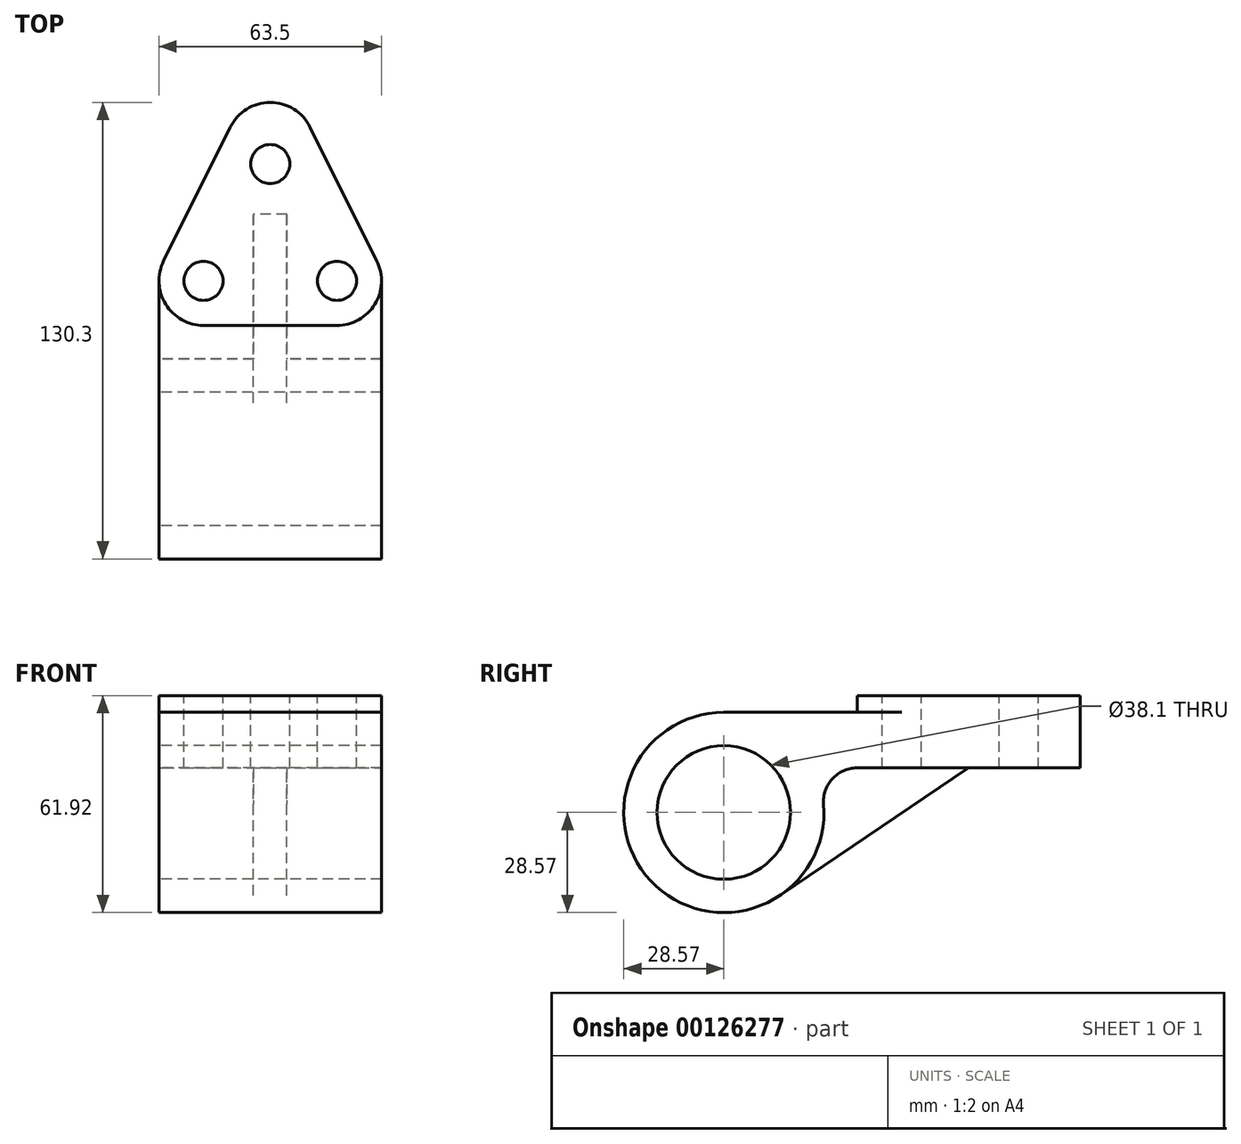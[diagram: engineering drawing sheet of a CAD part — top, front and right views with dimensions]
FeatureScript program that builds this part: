
annotation { "Feature Type Name" : "Feature", "Feature Type Description" : "" }
export const myFeature = defineFeature(function(context is Context, id is Id, definition is map)
    precondition{}
    {
        {
            var Q0;
            Q0=qCreatedBy(makeId("Right.planeOp"),FACE);
            var sketch = newSketch(context, id + "F0", { "sketchPlane" : qUnion([Q0])});
            skArc(sketch, "E0", {"start": v(0, 28.58) * mm, "mid": v(-19.35, -21.03) * mm, "end": v(28.48, 2.38) * mm});
            skCircle(sketch, "E1", {"center": v(0, 0) * mm, "radius": 19.05 * mm});
            skLineSegment(sketch, "E2", {"start": v(0, 28.58) * mm, "end": v(38.1, 28.58) * mm});
            skLineSegment(sketch, "E3", {"start": v(38.1, 28.58) * mm, "end": v(38.1, 33.35) * mm});
            skLineSegment(sketch, "E4", {"start": v(38.1, 33.35) * mm, "end": v(101.73, 33.35) * mm});
            skLineSegment(sketch, "E5", {"start": v(101.73, 33.35) * mm, "end": v(101.73, 12.7) * mm});
            skLineSegment(sketch, "E6", {"start": v(101.73, 12.7) * mm, "end": v(37.97, 12.7) * mm});
            skPoint(sketch, "E7.visualSharp", {"position": v(25.6, 12.7) * mm});
            skArc(sketch, "E7.filletArc", {"start": v(37.97, 12.7) * mm, "mid": v(30.96, 9.62) * mm, "end": v(28.48, 2.38) * mm});
            skLineSegment(sketch, "E8", {"start": v(69.85, 12.7) * mm, "end": v(69.85, 33.35) * mm, "construction": true});
            skLineSegment(sketch, "E9", {"start": v(16, -23.68) * mm, "end": v(69.85, 12.7) * mm});
            skSolve(sketch);
        }
        {
            var Q0;
            Q0=makeQuery(id+"F0.imprint","IMPRINT",FACE,{"disambiguationData":[TD([[makeQuery(id+"F0.imprint","IMPRINT",EDGE,{"derivedFrom":sQuery(id+"F0.wireOp",EDGE,"E1")}),-1.0]])]});
            extrude(context, id + "F1", {"entities" : qUnion([Q0]), "endBound" : BoundingType.SYMMETRIC, "depth" : 63.5 * mm});
        }
        {
            var Q0;
            Q0=makeQuery(id+"F1.opExtrude","SWEPT_FACE",FACE,{"disambiguationData":[OSD([sQuery(id+"F0.wireOp",EDGE,"E4")])]});
            var sketch = newSketch(context, id + "F2", { "sketchPlane" : qUnion([Q0])});
            skCircle(sketch, "E10", {"center": v(0, 84.15) * mm, "radius": 5.56 * mm});
            skCircle(sketch, "E11", {"center": v(-19.05, 50.8) * mm, "radius": 5.56 * mm});
            skCircle(sketch, "E12", {"center": v(19.05, 50.8) * mm, "radius": 5.56 * mm});
            skLineSegment(sketch, "E13", {"start": v(-19.05, 38.1) * mm, "end": v(19.05, 38.1) * mm});
            skArc(sketch, "E14", {"start": v(19.05, 38.1) * mm, "mid": v(29.85, 44.12) * mm, "end": v(30.42, 56.46) * mm});
            skArc(sketch, "E15", {"start": v(-30.42, 56.46) * mm, "mid": v(-29.85, 44.12) * mm, "end": v(-19.05, 38.1) * mm});
            skArc(sketch, "E16", {"start": v(11.37, 94.7) * mm, "mid": v(0, 101.73) * mm, "end": v(-11.37, 94.7) * mm});
            skLineSegment(sketch, "E17", {"start": v(-11.37, 94.7) * mm, "end": v(-30.42, 56.46) * mm});
            skLineSegment(sketch, "E18", {"start": v(30.42, 56.46) * mm, "end": v(11.37, 94.7) * mm});
            skSolve(sketch);
        }
        {
            var Q0;
            {var subQ0=sQuery(id+"F2.wireOp",EDGE,"E18");Q0=makeQuery(id+"F2.imprint","IMPRINT",FACE,{"disambiguationData":[TD([[makeQuery(id+"F2.imprint","IMPRINT",EDGE,{"derivedFrom":subQ0}),-1.0]])]});}
            extrude(context, id + "F3", {"entities" : qUnion([Q0]), "operationType" : NewBodyOperationType.REMOVE, "oppositeDirection" : true, "depth" : 43.07 * mm});
        }
        {
            var Q0;
            {var subQ0=sQuery(id+"F2.wireOp",EDGE,"E17");Q0=makeQuery(id+"F2.imprint","IMPRINT",FACE,{"disambiguationData":[TD([[makeQuery(id+"F2.imprint","IMPRINT",EDGE,{"derivedFrom":subQ0}),-1.0]])]});}
            extrude(context, id + "F4", {"entities" : qUnion([Q0]), "operationType" : NewBodyOperationType.REMOVE, "oppositeDirection" : true, "depth" : 25.4 * mm});
        }
        {
            var Q0;
            {var subQ0=sQuery(id+"F2.wireOp",EDGE,"E15");var subQ1=sQuery(id+"F0.wireOp",EDGE,"E4");var subQ4=makeQuery(id+"F1.opExtrude","CAP_EDGE",EDGE,{"disambiguationData":[OSD([subQ1])],"isStart":true});var subQ5=makeQuery(id+"F2.imprint","INTERSECT",VERTEX,{"derivedFrom":[subQ4,subQ0]});Q0=makeQuery(id+"F2.imprint","IMPRINT",FACE,{"disambiguationData":[TD([[makeQuery(id+"F2.imprint","IMPRINT",EDGE,{"disambiguationData":[TD([[subQ5,1.0]])],"derivedFrom":subQ4}),-1.0]])]});}
            extrude(context, id + "F5", {"entities" : qUnion([Q0]), "operationType" : NewBodyOperationType.REMOVE, "oppositeDirection" : true, "depth" : 4.78 * mm});
        }
        {
            var Q0;
            {var subQ0=sQuery(id+"F2.wireOp",EDGE,"E14");var subQ1=sQuery(id+"F0.wireOp",EDGE,"E4");var subQ4=makeQuery(id+"F1.opExtrude","CAP_EDGE",EDGE,{"disambiguationData":[OSD([subQ1])],"isStart":false});var subQ5=makeQuery(id+"F2.imprint","INTERSECT",VERTEX,{"derivedFrom":[subQ4,subQ0]});Q0=makeQuery(id+"F2.imprint","IMPRINT",FACE,{"disambiguationData":[TD([[makeQuery(id+"F2.imprint","IMPRINT",EDGE,{"disambiguationData":[TD([[subQ5,1.0]])],"derivedFrom":subQ4}),1.0]])]});}
            extrude(context, id + "F6", {"entities" : qUnion([Q0]), "operationType" : NewBodyOperationType.REMOVE, "oppositeDirection" : true, "depth" : 4.78 * mm});
        }
        {
            var Q0;
            Q0=makeQuery(id+"F2.imprint","IMPRINT",FACE,{"disambiguationData":[TD([[makeQuery(id+"F2.imprint","IMPRINT",EDGE,{"derivedFrom":sQuery(id+"F2.wireOp",EDGE,"E11")}),1.0]])]});
            var Q1;
            Q1=makeQuery(id+"F2.imprint","IMPRINT",FACE,{"disambiguationData":[TD([[makeQuery(id+"F2.imprint","IMPRINT",EDGE,{"derivedFrom":sQuery(id+"F2.wireOp",EDGE,"E10")}),1.0]])]});
            var Q2;
            Q2=makeQuery(id+"F2.imprint","IMPRINT",FACE,{"disambiguationData":[TD([[makeQuery(id+"F2.imprint","IMPRINT",EDGE,{"derivedFrom":sQuery(id+"F2.wireOp",EDGE,"E12")}),1.0]])]});
            extrude(context, id + "F7", {"entities" : qUnion([Q0, Q1, Q2]), "operationType" : NewBodyOperationType.REMOVE, "endBound" : BoundingType.THROUGH_ALL, "oppositeDirection" : true, "depth" : 25.4 * mm});
        }
        {
            var Q0;
            {var subQ0=sQuery(id+"F0.wireOp",EDGE,"E7.filletArc");Q0=makeQuery(id+"F0.imprint","IMPRINT",FACE,{"disambiguationData":[TD([[makeQuery(id+"F0.imprint","IMPRINT",EDGE,{"derivedFrom":subQ0}),1.0]])]});}
            extrude(context, id + "F8", {"entities" : qUnion([Q0]), "operationType" : NewBodyOperationType.ADD, "endBound" : BoundingType.SYMMETRIC, "depth" : 9.52 * mm});
        }
    });
